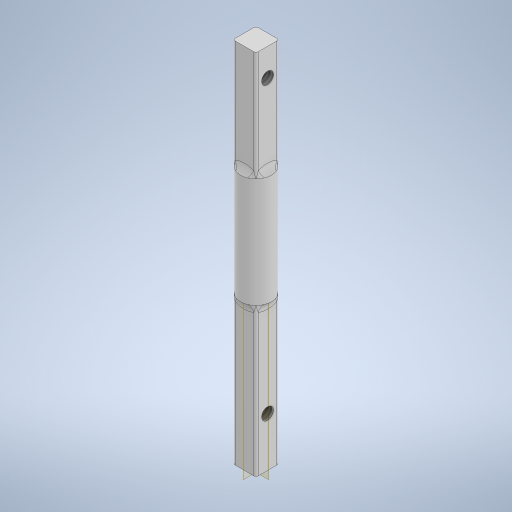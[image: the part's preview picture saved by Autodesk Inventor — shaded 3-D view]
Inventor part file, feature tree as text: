
AUTODESK INVENTOR PART (.ipt)
format: ipt  version: 2023.2 (Build 272271030, 271C)  size: 397,312 bytes
history: native  units: in
note: dims shown in document units (in); Inventor stores cm internally (conversion verified against a paired STEP export)
features: sketch x5, extrude x3, hole x2, fillet x2, plane x2, projected_geometry x2
ambient origin geometry x8: Origin, YZ Plane, XZ Plane, XY Plane, X Axis, Y Axis, Z Axis, Center Point
bodies: Solid1 (feature_tree)
feature tree (16):
  extrude  "Extrusion1"  Depth=1.063in TaperAngle=0.0deg
  hole  "Hole1"  [1 undecoded]
  fillet  "Fillet1"  Radius=0.7874in
  plane  "Work Plane1"
  plane  "Work Plane2"
  extrude  "Extrusion2"  Depth=0.1969in
  extrude  "Extrusion3"  Depth=0.0787in
  hole  "Hole3"  [1 undecoded]
  fillet  "Fillet2"  [1 undecoded]
  sketch  "Sketch1"  dims[d0=0.2343in d1=1.063in d2=0.0in]
  sketch  "Sketch2"  dims[d3=0.3543in]
  sketch  "Sketch3"  dims[d4=0.0849in d5=0.224in d6=0.1575in d7=0.0787in d8=90.0deg d9=0.315in d10=0.8108in d11=0.0157in d12=0.7874in d13=0.0in]
  projected_geometry  "Projected Loop1"
  sketch  "Sketch4"  dims[d14=0.7874in d15=0.0in d23=0.1969in]
  projected_geometry  "Projected Loop2"
  sketch  "Sketch6"  dims[d24=0.0849in d25=0.224in d26=0.1575in d27=0.0787in d28=90.0deg d29=0.349in d30=0.8108in d31=0.0787in]
note: 3 required parameter values undecoded (feature->parameter linkage not recoverable at this tier; creation-order binding heuristic only, values carry confidence <= 0.55)
